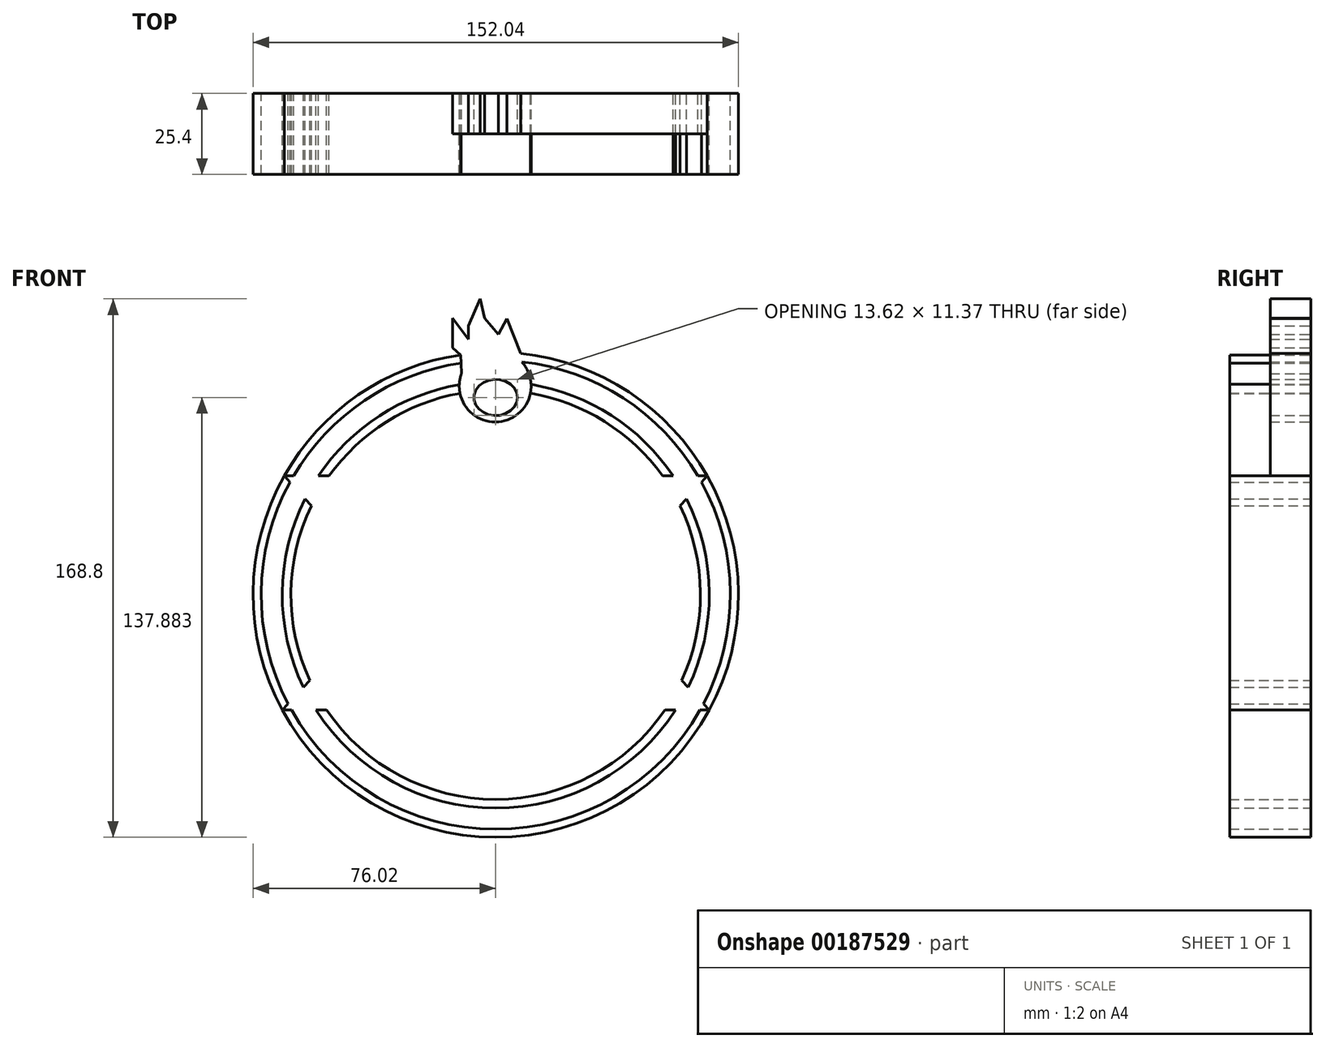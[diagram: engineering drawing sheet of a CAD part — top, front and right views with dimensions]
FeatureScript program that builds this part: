
annotation { "Feature Type Name" : "Feature", "Feature Type Description" : "" }
export const myFeature = defineFeature(function(context is Context, id is Id, definition is map)
    precondition{}
    {
        {
            var Q0;
            Q0=qCreatedBy(makeId("Front.planeOp"),FACE);
            var sketch = newSketch(context, id + "F0", { "sketchPlane" : qUnion([Q0])});
            skArc(sketch, "E0", {"start": v(-11.04, 75.21) * mm, "mid": v(1.6, -76) * mm, "end": v(7.85, 75.61) * mm});
            skArc(sketch, "E1", {"start": v(-11.42, 65.9) * mm, "mid": v(-36.99, 55.73) * mm, "end": v(-56.3, 36.13) * mm});
            skArc(sketch, "E2", {"start": v(-10.72, 69.35) * mm, "mid": v(1.95, 54.35) * mm, "end": v(8.16, 72.97) * mm});
            skPoint(sketch, "E2.first.point", {"position": v(-8.51, 72.97) * mm});
            skPoint(sketch, "E2.second.point", {"position": v(10.5, 61.86) * mm});
            skPoint(sketch, "E2.third.point", {"position": v(8.16, 72.97) * mm});
            skPoint(sketch, "E3.first.point", {"position": v(-4.88, 69.98) * mm});
            skPoint(sketch, "E3.second.point", {"position": v(4.95, 61.86) * mm});
            skPoint(sketch, "E3.third.point", {"position": v(-3.6, 61.22) * mm});
            skEllipse(sketch, "E4", {"center": v(0, 61.86) * mm, "majorRadius": 6.81 * mm, "minorRadius": 5.69 * mm, "majorAxis": v(1, 0)});
            skLineSegment(sketch, "E5", {"start": v(-11.02, 75.2) * mm, "end": v(-13.52, 77.41) * mm});
            skLineSegment(sketch, "E6", {"start": v(-13.52, 77.41) * mm, "end": v(-13.52, 86.7) * mm});
            skLineSegment(sketch, "E7", {"start": v(-13.52, 86.7) * mm, "end": v(-8.51, 80.13) * mm});
            skLineSegment(sketch, "E8", {"start": v(-8.51, 80.13) * mm, "end": v(-8.51, 84.3) * mm});
            skLineSegment(sketch, "E9", {"start": v(-8.51, 84.3) * mm, "end": v(-4.88, 92.78) * mm});
            skLineSegment(sketch, "E10", {"start": v(-4.88, 92.78) * mm, "end": v(-3.43, 86.7) * mm});
            skLineSegment(sketch, "E11", {"start": v(-3.43, 86.7) * mm, "end": v(0.84, 81.64) * mm});
            skLineSegment(sketch, "E12", {"start": v(0.84, 81.64) * mm, "end": v(3.45, 86.54) * mm});
            skLineSegment(sketch, "E13", {"start": v(3.45, 86.54) * mm, "end": v(5.9, 80.44) * mm});
            skLineSegment(sketch, "E14", {"start": v(5.9, 80.44) * mm, "end": v(7.85, 75.61) * mm});
            skLineSegment(sketch, "E15", {"start": v(7.85, 75.61) * mm, "end": v(8.16, 72.97) * mm});
            skLineSegment(sketch, "E16", {"start": v(-11.02, 75.2) * mm, "end": v(-10.72, 69.35) * mm});
            skLineSegment(sketch, "E17", {"start": v(-66.26, 37.26) * mm, "end": v(66.26, 37.26) * mm});
            skLineSegment(sketch, "E18", {"start": v(66.26, 37.26) * mm, "end": v(0, -36.13) * mm});
            skLineSegment(sketch, "E19", {"start": v(-66.26, 37.26) * mm, "end": v(0, -36.13) * mm});
            skLineSegment(sketch, "E20", {"start": v(-66.88, -36.13) * mm, "end": v(66.88, -36.13) * mm});
            skLineSegment(sketch, "E21", {"start": v(66.88, -36.13) * mm, "end": v(0, 36.13) * mm});
            skLineSegment(sketch, "E22", {"start": v(-66.88, -36.13) * mm, "end": v(0, 36.13) * mm});
            skPoint(sketch, "E23.orphan", {"position": v(-56.3, 36.13) * mm});
            skArc(sketch, "E24.trimOffspring", {"start": v(-59.76, 30.06) * mm, "mid": v(-66.89, 0.6) * mm, "end": v(-60.28, -29) * mm});
            skPoint(sketch, "E25.orphan", {"position": v(-56.3, -36.13) * mm});
            skArc(sketch, "E26.trimOffspring", {"start": v(-56.3, -36.13) * mm, "mid": v(0, -66.89) * mm, "end": v(56.3, -36.13) * mm});
            skPoint(sketch, "E27.orphan", {"position": v(56.3, -36.13) * mm});
            skArc(sketch, "E28.trimOffspring", {"start": v(60.28, -29) * mm, "mid": v(66.89, 0.6) * mm, "end": v(59.76, 30.06) * mm});
            skPoint(sketch, "E29.trimOffspring.end.orphan", {"position": v(56.3, 36.13) * mm});
            skPoint(sketch, "E30.orphan", {"position": v(35.67, 9.66) * mm});
            skPoint(sketch, "E31.end.orphan", {"position": v(0, 30.47) * mm});
            skPoint(sketch, "E32.end.orphan", {"position": v(-20.62, 4) * mm});
            skPoint(sketch, "E32.start.orphan", {"position": v(20.62, 4) * mm});
            skPoint(sketch, "E33.orphan", {"position": v(35.67, -9.66) * mm});
            skPoint(sketch, "E34.MirrorCS.end.orphan", {"position": v(20.62, -9.66) * mm});
            skPoint(sketch, "E35.MirrorCS.end.orphan", {"position": v(20.62, 9.66) * mm});
            skPoint(sketch, "E36.orphan", {"position": v(-20.62, 9.66) * mm});
            skPoint(sketch, "E37.orphan", {"position": v(-35.67, 9.66) * mm});
            skPoint(sketch, "E38.orphan", {"position": v(-35.67, -9.66) * mm});
            skArc(sketch, "E39.trimOffspring", {"start": v(56.3, 36.13) * mm, "mid": v(36.84, 55.83) * mm, "end": v(11.07, 65.97) * mm});
            skPoint(sketch, "E40.MirrorCS.end.orphan", {"position": v(-20.62, -9.66) * mm});
            skLineSegment(sketch, "E41", {"start": v(-41.34, 9.66) * mm, "end": v(-24.5, 9.66) * mm});
            skLineSegment(sketch, "E42.MirrorCS", {"start": v(-41.34, -9.66) * mm, "end": v(-24.5, -9.66) * mm});
            skLineSegment(sketch, "E43.MirrorCS", {"start": v(41.34, 9.66) * mm, "end": v(24.5, 9.66) * mm});
            skLineSegment(sketch, "E44.MirrorCS", {"start": v(41.34, -9.66) * mm, "end": v(24.5, -9.66) * mm});
            skLineSegment(sketch, "E45", {"start": v(0, 26.76) * mm, "end": v(-24.77, 0) * mm});
            skLineSegment(sketch, "E46", {"start": v(-24.77, 0) * mm, "end": v(0, 0) * mm});
            skLineSegment(sketch, "E47.MirrorCS", {"start": v(0, 26.76) * mm, "end": v(24.77, 0) * mm});
            skLineSegment(sketch, "E48.MirrorCS", {"start": v(24.77, 0) * mm, "end": v(0, 0) * mm});
            skEllipticalArc(sketch, "E49", {});
            skLineSegment(sketch, "E50", {"start": v(-27.09, -44.5) * mm, "end": v(-16.52, -44.5) * mm});
            skLineSegment(sketch, "E51", {"start": v(-16.52, -44.5) * mm, "end": v(-16.52, -40.8) * mm});
            skLineSegment(sketch, "E52", {"start": v(-16.52, -40.8) * mm, "end": v(-20.52, -37.11) * mm});
            skLineSegment(sketch, "E53", {"start": v(-20.52, -37.11) * mm, "end": v(-27.66, -39.73) * mm});
            skLineSegment(sketch, "E54", {"start": v(-27.18, -51.52) * mm, "end": v(-17.96, -51.52) * mm});
            skLineSegment(sketch, "E55", {"start": v(-17.96, -51.52) * mm, "end": v(-17.96, -56.26) * mm});
            skLineSegment(sketch, "E56", {"start": v(-17.96, -56.26) * mm, "end": v(-22.27, -59.13) * mm});
            skLineSegment(sketch, "E57", {"start": v(-22.27, -59.13) * mm, "end": v(-27.3, -56.26) * mm});
            skLineSegment(sketch, "E58", {"start": v(0, 56.18) * mm, "end": v(0, 54.15) * mm});
            skLineSegment(sketch, "E59", {"start": v(-33.02, 0.45) * mm, "end": v(-24.77, 0) * mm});
            skLineSegment(sketch, "E60", {"start": v(24.77, 0) * mm, "end": v(32.62, 0) * mm});
            skLineSegment(sketch, "E61", {"start": v(-16.76, 4) * mm, "end": v(0, 21.37) * mm});
            skLineSegment(sketch, "E62", {"start": v(0, 21.37) * mm, "end": v(16.76, 4) * mm});
            skLineSegment(sketch, "E63", {"start": v(-17.54, 4) * mm, "end": v(17.54, 4) * mm});
            skPoint(sketch, "E64.orphan", {"position": v(0, 26.76) * mm});
            skPoint(sketch, "E65.end.orphan", {"position": v(-20.62, 0) * mm});
            skPoint(sketch, "E66.MirrorCS.end.orphan", {"position": v(20.62, 0) * mm});
            skArc(sketch, "E67", {"start": v(-64.47, 35.28) * mm, "mid": v(-73.5, 0.63) * mm, "end": v(-65.07, -34.17) * mm});
            skArc(sketch, "E68", {"start": v(-57.77, 27.86) * mm, "mid": v(-64.14, 0.58) * mm, "end": v(-58.27, -26.82) * mm});
            skArc(sketch, "E69.trimOffspring", {"start": v(-53, -36.13) * mm, "mid": v(0, -64.14) * mm, "end": v(53, -36.13) * mm});
            skArc(sketch, "E70.trimOffspring", {"start": v(-64, -36.13) * mm, "mid": v(0, -73.5) * mm, "end": v(64, -36.13) * mm});
            skArc(sketch, "E71.trimOffspring", {"start": v(58.27, -26.82) * mm, "mid": v(64.14, 0.58) * mm, "end": v(57.77, 27.86) * mm});
            skArc(sketch, "E72.trimOffspring", {"start": v(65.07, -34.17) * mm, "mid": v(73.5, 0.63) * mm, "end": v(64.47, 35.28) * mm});
            skArc(sketch, "E73.trimOffspring", {"start": v(52.2, 37.26) * mm, "mid": v(34.1, 54.33) * mm, "end": v(10.86, 63.22) * mm});
            skArc(sketch, "E74.trimOffspring", {"start": v(63.35, 37.26) * mm, "mid": v(39.97, 61.67) * mm, "end": v(8.15, 73.04) * mm});
            skArc(sketch, "E75.trimOffspring", {"start": v(-11.2, 63.16) * mm, "mid": v(-34.25, 54.23) * mm, "end": v(-52.2, 37.26) * mm});
            skArc(sketch, "E76.trimOffspring", {"start": v(-10.89, 72.68) * mm, "mid": v(-41.13, 60.9) * mm, "end": v(-63.35, 37.26) * mm});
            skCircle(sketch, "E77", {"center": v(-4.58, 97.36) * mm, "radius": 4.59 * mm});
            skPoint(sketch, "E77.first.point", {"position": v(-5.38, 101.87) * mm});
            skPoint(sketch, "E77.third.point", {"position": v(0, 97.2) * mm});
            skArc(sketch, "E78", {"start": v(-3.43, 86.7) * mm, "mid": v(-3.54, 103.38) * mm, "end": v(-7.3, 87.13) * mm});
            skPoint(sketch, "E78.first.point", {"position": v(-12.2, 98.28) * mm});
            skPoint(sketch, "E78.second.point", {"position": v(3.6, 97.36) * mm});
            skLineSegment(sketch, "E79", {"start": v(-16.52, -44.5) * mm, "end": v(0, -44.5) * mm});
            skLineSegment(sketch, "E80", {"start": v(0, -44.5) * mm, "end": v(2.53, -40.8) * mm});
            skLineSegment(sketch, "E81", {"start": v(-5.02, -40.8) * mm, "end": v(2.53, -40.8) * mm});
            skLineSegment(sketch, "E82", {"start": v(-17.96, -51.52) * mm, "end": v(0, -51.52) * mm});
            skLineSegment(sketch, "E83", {"start": v(0, -51.52) * mm, "end": v(2.41, -54.4) * mm});
            skLineSegment(sketch, "E84", {"start": v(2.41, -54.4) * mm, "end": v(-2.67, -58.66) * mm});
            skLineSegment(sketch, "E85", {"start": v(-2.67, -58.66) * mm, "end": v(-6.98, -59.76) * mm});
            skLineSegment(sketch, "E86", {"start": v(-6.98, -59.76) * mm, "end": v(-5.92, -63.87) * mm});
            skLineSegment(sketch, "E87", {"start": v(-5.92, -63.87) * mm, "end": v(0, -62.35) * mm});
            skLineSegment(sketch, "E88", {"start": v(0, -62.35) * mm, "end": v(4.83, -55.74) * mm});
            skLineSegment(sketch, "E89", {"start": v(4.83, -55.74) * mm, "end": v(3.49, -51.52) * mm});
            skLineSegment(sketch, "E90", {"start": v(3.49, -51.52) * mm, "end": v(8.85, -46.62) * mm});
            skLineSegment(sketch, "E91", {"start": v(8.85, -46.62) * mm, "end": v(12.56, -45.44) * mm});
            skLineSegment(sketch, "E92", {"start": v(12.56, -45.44) * mm, "end": v(17.44, -45.44) * mm});
            skLineSegment(sketch, "E93", {"start": v(17.44, -45.44) * mm, "end": v(22.27, -51.52) * mm});
            skLineSegment(sketch, "E94", {"start": v(22.27, -51.52) * mm, "end": v(22.27, -54.67) * mm});
            const initialGuessF0  = {"E49": [-0.031974706798791885, -0.047991618514060974, 1, 0, 0.00826575793325901, 0.0043289650518683965, 0.9383863801674102, 5.330889094724162]};
            skSetInitialGuess(sketch, initialGuessF0);
            skSolve(sketch);
        }
        {
            var Q0;
            {var subQ5=sQuery(id+"F0.wireOp",EDGE,"E74.trimOffspring");Q0=makeQuery(id+"F0.imprint","IMPRINT",FACE,{"disambiguationData":[TD([[makeQuery(id+"F0.imprint","IMPRINT",EDGE,{"derivedFrom":subQ5}),-1.0]])]});}
            extrude(context, id + "F1", {"entities" : qUnion([Q0]), "depth" : 12.7 * mm});
        }
        {
            var Q0;
            Q0=makeQuery(id+"F0.imprint","IMPRINT",FACE,{"disambiguationData":[TD([[makeQuery(id+"F0.imprint","IMPRINT",EDGE,{"derivedFrom":sQuery(id+"F0.wireOp",EDGE,"E4")}),-1.0]])]});
            extrude(context, id + "F2", {"entities" : qUnion([Q0]), "operationType" : NewBodyOperationType.ADD, "depth" : 12.7 * mm});
        }
        {
            var Q0;
            {var subQ3=sQuery(id+"F0.wireOp",EDGE,"E76.trimOffspring");Q0=makeQuery(id+"F0.imprint","IMPRINT",FACE,{"disambiguationData":[TD([[makeQuery(id+"F0.imprint","IMPRINT",EDGE,{"derivedFrom":subQ3}),-1.0]])]});}
            var Q1;
            {var subQ5=sQuery(id+"F0.wireOp",EDGE,"E75.trimOffspring");Q1=makeQuery(id+"F0.imprint","IMPRINT",FACE,{"disambiguationData":[TD([[makeQuery(id+"F0.imprint","IMPRINT",EDGE,{"derivedFrom":subQ5}),-1.0]])]});}
            var Q2;
            {var subQ3=sQuery(id+"F0.wireOp",EDGE,"E73.trimOffspring");Q2=makeQuery(id+"F0.imprint","IMPRINT",FACE,{"disambiguationData":[TD([[makeQuery(id+"F0.imprint","IMPRINT",EDGE,{"derivedFrom":subQ3}),-1.0]])]});}
            var Q3;
            {var subQ5=sQuery(id+"F0.wireOp",EDGE,"E67");Q3=makeQuery(id+"F0.imprint","IMPRINT",FACE,{"disambiguationData":[TD([[makeQuery(id+"F0.imprint","IMPRINT",EDGE,{"derivedFrom":subQ5}),-1.0]])]});}
            var Q4;
            {var subQ0=sQuery(id+"F0.wireOp",EDGE,"E24.trimOffspring");Q4=makeQuery(id+"F0.imprint","IMPRINT",FACE,{"disambiguationData":[TD([[makeQuery(id+"F0.imprint","IMPRINT",EDGE,{"derivedFrom":subQ0}),1.0]])]});}
            var Q5;
            {var subQ4=sQuery(id+"F0.wireOp",EDGE,"E70.trimOffspring");Q5=makeQuery(id+"F0.imprint","IMPRINT",FACE,{"disambiguationData":[TD([[makeQuery(id+"F0.imprint","IMPRINT",EDGE,{"derivedFrom":subQ4}),-1.0]])]});}
            var Q6;
            {var subQ0=sQuery(id+"F0.wireOp",EDGE,"E26.trimOffspring");Q6=makeQuery(id+"F0.imprint","IMPRINT",FACE,{"disambiguationData":[TD([[makeQuery(id+"F0.imprint","IMPRINT",EDGE,{"derivedFrom":subQ0}),1.0]])]});}
            var Q7;
            {var subQ0=sQuery(id+"F0.wireOp",EDGE,"E28.trimOffspring");Q7=makeQuery(id+"F0.imprint","IMPRINT",FACE,{"disambiguationData":[TD([[makeQuery(id+"F0.imprint","IMPRINT",EDGE,{"derivedFrom":subQ0}),1.0]])]});}
            var Q8;
            {var subQ5=sQuery(id+"F0.wireOp",EDGE,"E72.trimOffspring");Q8=makeQuery(id+"F0.imprint","IMPRINT",FACE,{"disambiguationData":[TD([[makeQuery(id+"F0.imprint","IMPRINT",EDGE,{"derivedFrom":subQ5}),-1.0]])]});}
            extrude(context, id + "F3", {"entities" : qUnion([Q0, Q1, Q2, Q3, Q4, Q5, Q6, Q7, Q8]), "operationType" : NewBodyOperationType.ADD, "depth" : 25.4 * mm});
        }
    });
